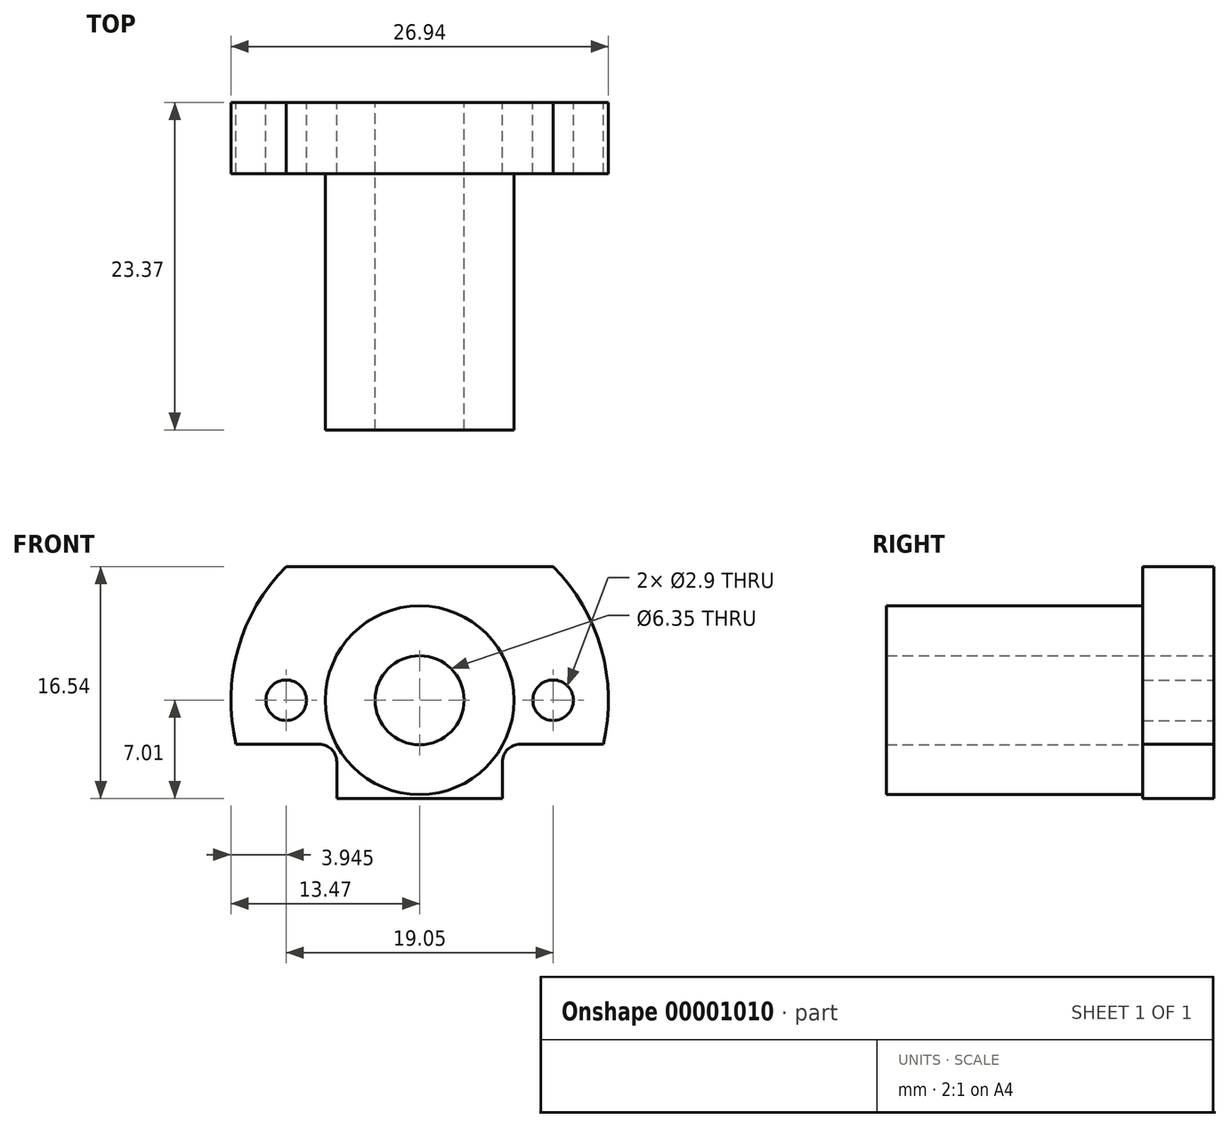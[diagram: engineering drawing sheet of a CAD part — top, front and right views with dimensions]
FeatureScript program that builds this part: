
annotation { "Feature Type Name" : "Feature", "Feature Type Description" : "" }
export const myFeature = defineFeature(function(context is Context, id is Id, definition is map)
    precondition{}
    {
        {
            var Q0;
            Q0=qCreatedBy(makeId("Front.planeOp"),FACE);
            var sketch = newSketch(context, id + "F0", { "sketchPlane" : qUnion([Q0])});
            skLineSegment(sketch, "E0.bottom", {"start": v(-9.53, 9.53) * mm, "end": v(9.53, 9.53) * mm});
            skLineSegment(sketch, "E0.top", {"start": v(-9.52, -9.53) * mm, "end": v(9.53, -9.52) * mm});
            skCircle(sketch, "E1", {"center": v(-9.53, 0) * mm, "radius": 1.45 * mm});
            skCircle(sketch, "E2", {"center": v(9.53, 0) * mm, "radius": 1.45 * mm});
            skArc(sketch, "E3", {"start": v(-9.53, 9.52) * mm, "mid": v(-13.47, 0) * mm, "end": v(-9.52, -9.53) * mm});
            skArc(sketch, "E4.trimOffspring", {"start": v(9.52, -9.52) * mm, "mid": v(13.47, 0) * mm, "end": v(9.52, 9.53) * mm});
            skCircle(sketch, "E5", {"center": v(0, 0) * mm, "radius": 3.18 * mm});
            skSolve(sketch);
        }
        {
            var Q0;
            Q0=makeQuery(id+"F0.imprint","IMPRINT",FACE,{"disambiguationData":[TD([[makeQuery(id+"F0.imprint","IMPRINT",EDGE,{"derivedFrom":sQuery(id+"F0.wireOp",EDGE,"E0.bottom")}),-1.0]])]});
            extrude(context, id + "F1", {"entities" : qUnion([Q0]), "depth" : 5.08 * mm});
        }
        {
            var Q0;
            Q0=makeQuery(id+"F1.opExtrude","CAP_FACE",FACE,{"disambiguationData":[OSD([sQuery(id+"F0.wireOp",EDGE,"E0.bottom"),sQuery(id+"F0.wireOp",EDGE,"E0.top"),sQuery(id+"F0.wireOp",EDGE,"E1"),sQuery(id+"F0.wireOp",EDGE,"E2"),sQuery(id+"F0.wireOp",EDGE,"E3"),sQuery(id+"F0.wireOp",EDGE,"E4.trimOffspring"),sQuery(id+"F0.wireOp",EDGE,"E5")])],"isStart":false});
            var sketch = newSketch(context, id + "F2", { "sketchPlane" : qUnion([Q0])});
            skCircle(sketch, "E6", {"center": v(0, 0) * mm, "radius": 6.73 * mm});
            skCircle(sketch, "E7", {"center": v(0, 0) * mm, "radius": 3.18 * mm});
            skSolve(sketch);
        }
        {
            var Q0;
            Q0=makeQuery(id+"F2.imprint","IMPRINT",FACE,{"disambiguationData":[TD([[makeQuery(id+"F2.imprint","IMPRINT",EDGE,{"derivedFrom":sQuery(id+"F2.wireOp",EDGE,"E6")}),1.0]])]});
            extrude(context, id + "F3", {"entities" : qUnion([Q0]), "operationType" : NewBodyOperationType.ADD, "depth" : 18.29 * mm});
        }
        {
            var Q0;
            Q0=makeQuery(id+"F1.opExtrude","CAP_FACE",FACE,{"disambiguationData":[OSD([sQuery(id+"F0.wireOp",EDGE,"E0.bottom"),sQuery(id+"F0.wireOp",EDGE,"E0.top"),sQuery(id+"F0.wireOp",EDGE,"E1"),sQuery(id+"F0.wireOp",EDGE,"E2"),sQuery(id+"F0.wireOp",EDGE,"E3"),sQuery(id+"F0.wireOp",EDGE,"E4.trimOffspring"),sQuery(id+"F0.wireOp",EDGE,"E5")])],"isStart":true});
            var sketch = newSketch(context, id + "F4", { "sketchPlane" : qUnion([Q0])});
            skLineSegment(sketch, "E8.bottom", {"start": v(-7.18, -3.13) * mm, "end": v(-14.21, -3.13) * mm});
            skLineSegment(sketch, "E8.top", {"start": v(-5.91, -10.74) * mm, "end": v(-14.21, -10.74) * mm});
            skLineSegment(sketch, "E8.left", {"start": v(-5.91, -4.4) * mm, "end": v(-5.91, -7) * mm});
            skLineSegment(sketch, "E8.right", {"start": v(-14.21, -3.13) * mm, "end": v(-14.21, -10.74) * mm});
            skLineSegment(sketch, "E9.0.MirrorCS", {"start": v(5.91, -4.4) * mm, "end": v(5.91, -7) * mm});
            skLineSegment(sketch, "E9.1.MirrorCS", {"start": v(5.91, -10.74) * mm, "end": v(14.21, -10.74) * mm});
            skLineSegment(sketch, "E9.2.MirrorCS", {"start": v(14.21, -3.13) * mm, "end": v(14.21, -10.74) * mm});
            skLineSegment(sketch, "E9.3.MirrorCS", {"start": v(7.18, -3.13) * mm, "end": v(14.21, -3.13) * mm});
            skPoint(sketch, "E10.visualSharp", {"position": v(5.91, -3.13) * mm});
            skArc(sketch, "E10.filletArc", {"start": v(7.18, -3.13) * mm, "mid": v(6.29, -3.5) * mm, "end": v(5.91, -4.4) * mm});
            skPoint(sketch, "E11.visualSharp", {"position": v(-5.91, -3.13) * mm});
            skArc(sketch, "E11.filletArc", {"start": v(-5.91, -4.4) * mm, "mid": v(-6.29, -3.5) * mm, "end": v(-7.18, -3.13) * mm});
            skLineSegment(sketch, "E12", {"start": v(5.91, -7) * mm, "end": v(-5.91, -7) * mm});
            skLineSegment(sketch, "E13", {"start": v(5.91, -10.74) * mm, "end": v(-5.91, -10.74) * mm});
            skSolve(sketch);
        }
        {
            var Q0;
            {var subQ1=sQuery(id+"F4.wireOp",EDGE,"E8.bottom");var subQ5=sQuery(id+"F4.wireOp",EDGE,"E8.left");var subQ7=makeQuery(id+"F4.imprint","INTERSECT",VERTEX,{"derivedFrom":[subQ1,subQ5]});Q0=makeQuery(id+"F4.imprint","IMPRINT",FACE,{"disambiguationData":[TD([[makeQuery(id+"F4.imprint","IMPRINT",EDGE,{"disambiguationData":[TD([[subQ7,-1.0]])],"derivedFrom":subQ1}),1.0]])]});}
            var Q1;
            {var subQ1=sQuery(id+"F4.wireOp",EDGE,"E9.0.MirrorCS");var subQ5=sQuery(id+"F4.wireOp",EDGE,"E9.3.MirrorCS");var subQ7=makeQuery(id+"F4.imprint","INTERSECT",VERTEX,{"derivedFrom":[subQ1,subQ5]});Q1=makeQuery(id+"F4.imprint","IMPRINT",FACE,{"disambiguationData":[TD([[makeQuery(id+"F4.imprint","IMPRINT",EDGE,{"disambiguationData":[TD([[subQ7,-1.0]])],"derivedFrom":subQ1}),1.0]])]});}
            extrude(context, id + "F5", {"entities" : qUnion([Q0, Q1]), "operationType" : NewBodyOperationType.REMOVE, "endBound" : BoundingType.THROUGH_ALL, "oppositeDirection" : true, "depth" : 25.4 * mm});
        }
    });
